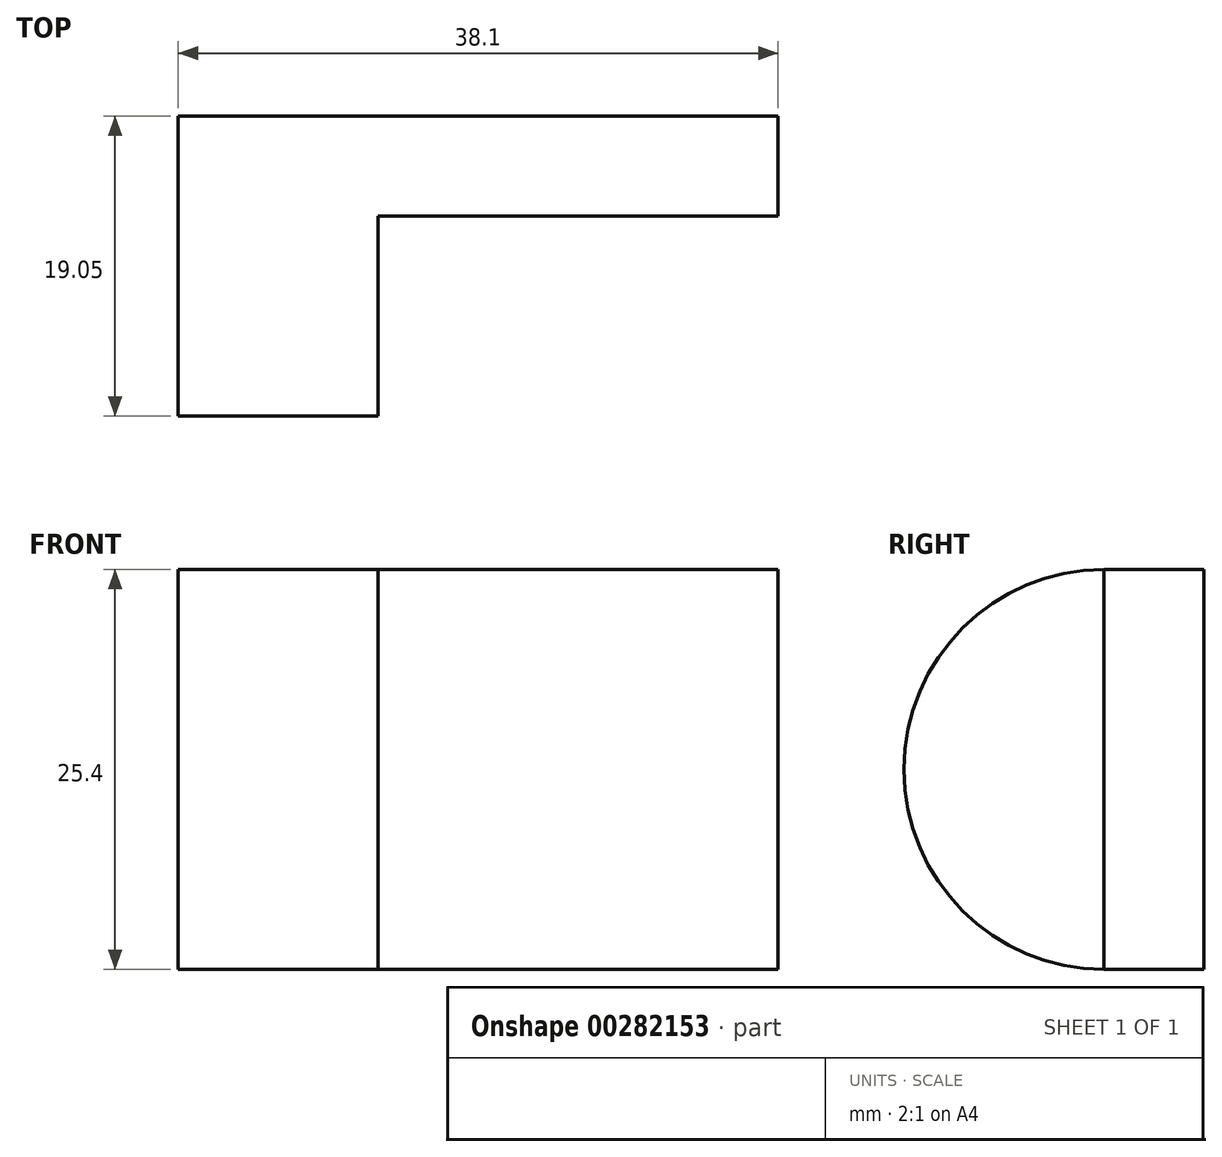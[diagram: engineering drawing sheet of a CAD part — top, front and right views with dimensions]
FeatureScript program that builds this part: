
annotation { "Feature Type Name" : "Feature", "Feature Type Description" : "" }
export const myFeature = defineFeature(function(context is Context, id is Id, definition is map)
    precondition{}
    {
        {
            var Q0;
            Q0=qCreatedBy(makeId("Front.planeOp"),FACE);
            var sketch = newSketch(context, id + "F0", { "sketchPlane" : qUnion([Q0])});
            skLineSegment(sketch, "E0", {"start": v(0, 0) * mm, "end": v(38.1, 0) * mm});
            skLineSegment(sketch, "E1", {"start": v(38.1, 0) * mm, "end": v(38.1, 25.4) * mm});
            skLineSegment(sketch, "E2", {"start": v(38.1, 25.4) * mm, "end": v(0, 25.4) * mm});
            skLineSegment(sketch, "E3", {"start": v(0, 25.4) * mm, "end": v(0, 0) * mm});
            skSolve(sketch);
        }
        {
            var Q0;
            Q0=makeQuery(id+"F0.imprint","IMPRINT",FACE,{"disambiguationData":[TD([[makeQuery(id+"F0.imprint","IMPRINT",EDGE,{"derivedFrom":sQuery(id+"F0.wireOp",EDGE,"E0")}),1.0]])]});
            extrude(context, id + "F1", {"entities" : qUnion([Q0]), "depth" : 6.35 * mm});
        }
        {
            var Q0;
            Q0=makeQuery(id+"F1.opExtrude","SWEPT_FACE",FACE,{"disambiguationData":[OSD([sQuery(id+"F0.wireOp",EDGE,"E3")])]});
            var sketch = newSketch(context, id + "F2", { "sketchPlane" : qUnion([Q0])});
            skArc(sketch, "E4", {"start": v(6.35, 0) * mm, "mid": v(19.05, 12.7) * mm, "end": v(6.35, 25.4) * mm});
            skSolve(sketch);
        }
        {
            var Q0;
            Q0=makeQuery(id+"F2.imprint","IMPRINT",FACE,{"disambiguationData":[TD([[makeQuery(id+"F2.imprint","IMPRINT",EDGE,{"derivedFrom":sQuery(id+"F2.wireOp",EDGE,"E4")}),1.0]])]});
            extrude(context, id + "F3", {"entities" : qUnion([Q0]), "operationType" : NewBodyOperationType.ADD, "oppositeDirection" : true, "depth" : 12.7 * mm});
        }
    });
